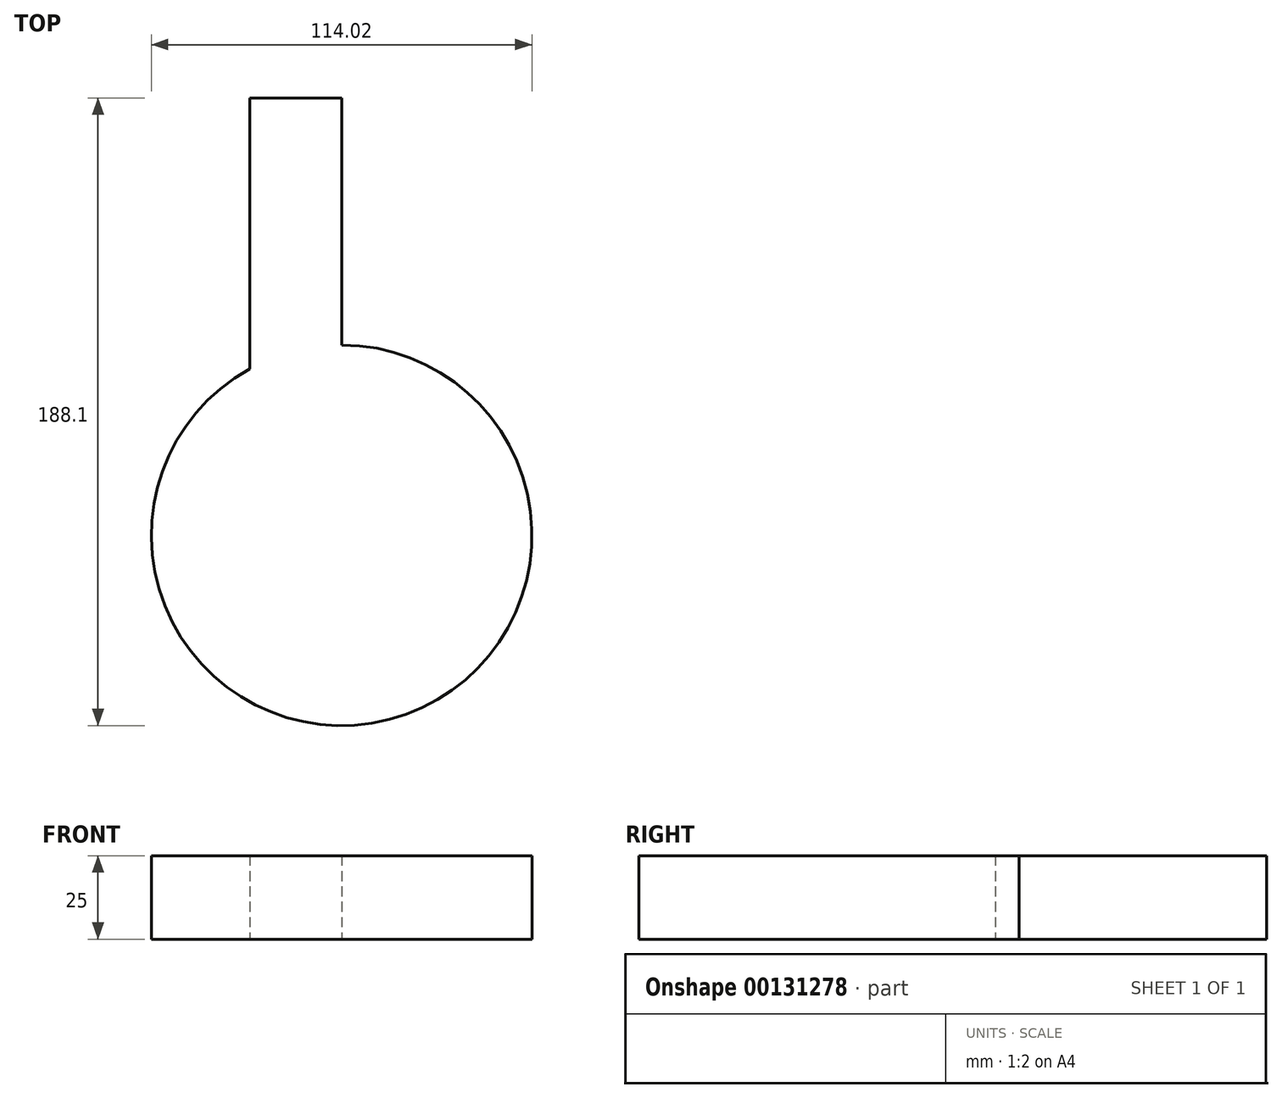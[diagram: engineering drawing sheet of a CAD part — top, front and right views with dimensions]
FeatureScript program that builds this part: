
annotation { "Feature Type Name" : "Feature", "Feature Type Description" : "" }
export const myFeature = defineFeature(function(context is Context, id is Id, definition is map)
    precondition{}
    {
        {
            var Q0;
            Q0=qCreatedBy(makeId("Top.planeOp"),FACE);
            var sketch = newSketch(context, id + "F0", { "sketchPlane" : qUnion([Q0])});
            skArc(sketch, "E0", {"start": v(-27.58, 17.36) * mm, "mid": v(14.24, -87.74) * mm, "end": v(0, 24.48) * mm});
            skPoint(sketch, "E1.left.start.orphan", {"position": v(0, 41.02) * mm});
            skLineSegment(sketch, "E2.top", {"start": v(0, 98.55) * mm, "end": v(-27.58, 98.55) * mm});
            skLineSegment(sketch, "E2.left", {"start": v(0, 24.48) * mm, "end": v(0, 98.55) * mm});
            skLineSegment(sketch, "E2.right", {"start": v(-27.58, 17.36) * mm, "end": v(-27.58, 98.55) * mm});
            skLineSegment(sketch, "E3", {"start": v(56.82, 30.18) * mm, "end": v(-66.72, 30.18) * mm, "construction": true});
            skSolve(sketch);
        }
        {
            var Q0;
            {var subQ0=sQuery(id+"F0.wireOp",EDGE,"E0");Q0=makeQuery(id+"F0.imprint","IMPRINT",FACE,{"disambiguationData":[TD([[makeQuery(id+"F0.imprint","IMPRINT",EDGE,{"derivedFrom":subQ0}),1.0]])]});}
            extrude(context, id + "F1", {"entities" : qUnion([Q0]), "depth" : 25 * mm});
        }
    });
